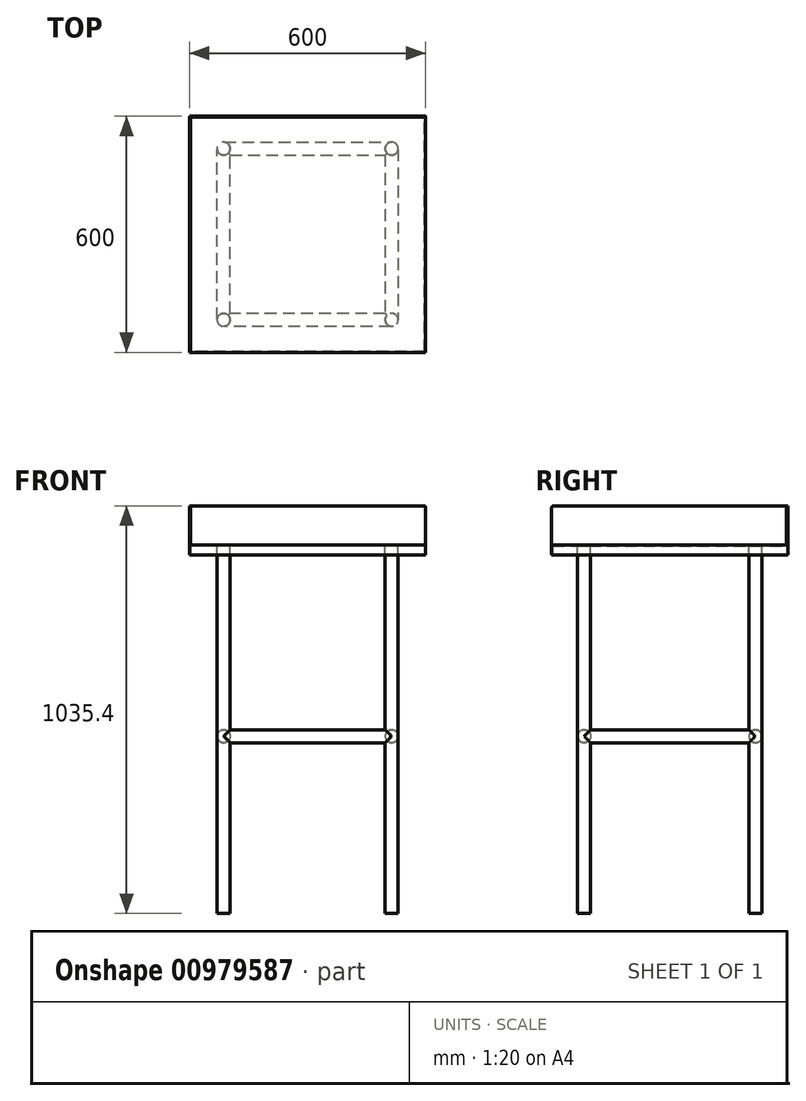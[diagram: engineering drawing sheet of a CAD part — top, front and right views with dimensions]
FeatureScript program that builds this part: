
annotation { "Feature Type Name" : "Feature", "Feature Type Description" : "" }
export const myFeature = defineFeature(function(context is Context, id is Id, definition is map)
    precondition{}
    {
        {
            var Q0;
            Q0=qCreatedBy(makeId("Top.planeOp"),FACE);
            var sketch = newSketch(context, id + "F0", { "sketchPlane" : qUnion([Q0])});
            skLineSegment(sketch, "E0.bottom", {"start": v(300, -300) * mm, "end": v(-300, -300) * mm});
            skLineSegment(sketch, "E0.top", {"start": v(300, 300) * mm, "end": v(-300, 300) * mm});
            skLineSegment(sketch, "E0.left", {"start": v(300, -300) * mm, "end": v(300, 300) * mm});
            skLineSegment(sketch, "E0.right", {"start": v(-300, -300) * mm, "end": v(-300, 300) * mm});
            skPoint(sketch, "E0.middle", {"position": v(0, 0) * mm});
            skSolve(sketch);
        }
        {
            var Q0;
            Q0 = qSketchRegion(id + "F0", true);
            extrude(context, id + "F1", {"entities" : qUnion([Q0]), "depth" : 25.4 * mm, "offsetDistance" : 25.4 * mm});
        }
        {
            var Q0;
            Q0=makeQuery(id+"F1.opExtrude","CAP_FACE",FACE,{"disambiguationData":[OSD([sQuery(id+"F0.wireOp",EDGE,"E0.bottom"),sQuery(id+"F0.wireOp",EDGE,"E0.top"),sQuery(id+"F0.wireOp",EDGE,"E0.left"),sQuery(id+"F0.wireOp",EDGE,"E0.right")])],"isStart":true});
            shell(context, id + "F2", {"entities" : qUnion([Q0]), "thickness" : 2.54 * mm});
        }
        {
            var Q0;
            Q0=makeQuery(id+"F1.opExtrude","CAP_FACE",FACE,{"disambiguationData":[OSD([sQuery(id+"F0.wireOp",EDGE,"E0.bottom"),sQuery(id+"F0.wireOp",EDGE,"E0.top"),sQuery(id+"F0.wireOp",EDGE,"E0.left"),sQuery(id+"F0.wireOp",EDGE,"E0.right")])],"isStart":true});
            var sketch = newSketch(context, id + "F3", { "sketchPlane" : qUnion([Q0])});
            skCircle(sketch, "E1", {"center": v(213.5, -217.5) * mm, "radius": 16.5 * mm});
            skCircle(sketch, "E2", {"center": v(-213.5, -217.5) * mm, "radius": 16.5 * mm});
            skCircle(sketch, "E3", {"center": v(213.5, 217.5) * mm, "radius": 16.5 * mm});
            skCircle(sketch, "E4", {"center": v(-213.5, 217.5) * mm, "radius": 16.5 * mm});
            skSolve(sketch);
        }
        {
            var Q0;
            Q0 = qSketchRegion(id + "F3", true);
            extrude(context, id + "F4", {"entities" : qUnion([Q0]), "operationType" : NewBodyOperationType.ADD, "depth" : 910 * mm, "offsetDistance" : 25.4 * mm, "hasSecondDirection" : true, "secondDirectionBound" : SecondDirectionBoundingType.UP_TO_NEXT, "secondDirectionOppositeDirection" : true, "secondDirectionDepth" : 25.4 * mm});
        }
        {
            var Q0;
            Q0=makeQuery(id+"F1.opExtrude","CAP_FACE",FACE,{"disambiguationData":[OSD([sQuery(id+"F0.wireOp",EDGE,"E0.bottom"),sQuery(id+"F0.wireOp",EDGE,"E0.top"),sQuery(id+"F0.wireOp",EDGE,"E0.left"),sQuery(id+"F0.wireOp",EDGE,"E0.right")])],"isStart":false});
            var sketch = newSketch(context, id + "F5", { "sketchPlane" : qUnion([Q0])});
            skLineSegment(sketch, "E5.bottom", {"start": v(-300, -300) * mm, "end": v(-297, -300) * mm});
            skLineSegment(sketch, "E5.top", {"start": v(-300, 300) * mm, "end": v(-297, 300) * mm});
            skLineSegment(sketch, "E5.left", {"start": v(-300, -300) * mm, "end": v(-300, 300) * mm});
            skLineSegment(sketch, "E5.right", {"start": v(-297, -300) * mm, "end": v(-297, 297) * mm});
            skLineSegment(sketch, "E6.bottom", {"start": v(-297, 300) * mm, "end": v(300, 300) * mm});
            skLineSegment(sketch, "E6.top", {"start": v(-297, 297) * mm, "end": v(300, 297) * mm});
            skLineSegment(sketch, "E6.right", {"start": v(300, 300) * mm, "end": v(300, 297) * mm});
            skSolve(sketch);
        }
        {
            var Q0;
            Q0 = qSketchRegion(id + "F5", true);
            extrude(context, id + "F6", {"entities" : qUnion([Q0]), "operationType" : NewBodyOperationType.ADD, "depth" : 100 * mm, "offsetDistance" : 25.4 * mm});
        }
        {
            var Q0;
            Q0=makeQuery(id+"F6.opExtrude","CAP_EDGE",EDGE,{"disambiguationData":[OSD([sQuery(id+"F5.wireOp",EDGE,"E6.right")])],"isStart":false});
            fillet(context, id + "F7", {"entities" : qUnion([Q0]), "radius" : 5.08 * mm, "tangentPropagation" : true, "allowEdgeOverflow" : false});
        }
        {
            var Q0;
            Q0=makeQuery(id+"F6.opExtrude","CAP_EDGE",EDGE,{"disambiguationData":[OSD([sQuery(id+"F5.wireOp",EDGE,"E5.bottom")])],"isStart":false});
            fillet(context, id + "F8", {"entities" : qUnion([Q0]), "radius" : 5.08 * mm, "tangentPropagation" : true, "allowEdgeOverflow" : false});
        }
        {
            var Q0;
            Q0=makeQuery(id+"F4.opExtrude","CAP_EDGE",EDGE,{"disambiguationData":[OSD([sQuery(id+"F3.wireOp",EDGE,"E2")])],"isStart":false});
            cPlane(context, id + "F9", {"entities" : qUnion([Q0]), "cplaneType" : CPlaneType.LINE_ANGLE, "offset" : 25.4 * mm, "angle" : 90 * degree, "width" : 152.4 * mm, "height" : 152.4 * mm});
        }
        {
            var Q0;
            Q0=qCreatedBy(id+"F9.planeOp",FACE);
            var sketch = newSketch(context, id + "F10", { "sketchPlane" : qUnion([Q0])});
            skCircle(sketch, "E7", {"center": v(213.49, -460) * mm, "radius": 16.5 * mm});
            skSolve(sketch);
        }
        {
            var Q0;
            Q0 = qSketchRegion(id + "F10", true);
            extrude(context, id + "F11", {"entities" : qUnion([Q0]), "operationType" : NewBodyOperationType.ADD, "oppositeDirection" : true, "depth" : 433.32 * mm, "offsetDistance" : 25.4 * mm});
        }
        {
            var Q0;
            Q0=makeQuery(id+"F4.opExtrude","CAP_EDGE",EDGE,{"disambiguationData":[OSD([sQuery(id+"F3.wireOp",EDGE,"E4")])],"isStart":false});
            cPlane(context, id + "F12", {"entities" : qUnion([Q0]), "cplaneType" : CPlaneType.LINE_ANGLE, "offset" : 25.4 * mm, "angle" : 0 * degree, "width" : 152.4 * mm, "height" : 152.4 * mm});
        }
        {
            var Q0;
            Q0=qCreatedBy(id+"F12.planeOp",FACE);
            var sketch = newSketch(context, id + "F13", { "sketchPlane" : qUnion([Q0])});
            skCircle(sketch, "E8", {"center": v(217.47, -460) * mm, "radius": 16.5 * mm});
            skSolve(sketch);
        }
        {
            var Q0;
            Q0 = qSketchRegion(id + "F13", true);
            extrude(context, id + "F14", {"entities" : qUnion([Q0]), "operationType" : NewBodyOperationType.ADD, "oppositeDirection" : true, "depth" : 424.43 * mm, "offsetDistance" : 25.4 * mm});
        }
        {
            var Q0;
            Q0=makeQuery(id+"F4.opExtrude","CAP_EDGE",EDGE,{"disambiguationData":[OSD([sQuery(id+"F3.wireOp",EDGE,"E3")])],"isStart":false});
            cPlane(context, id + "F15", {"entities" : qUnion([Q0]), "cplaneType" : CPlaneType.LINE_ANGLE, "offset" : 25.4 * mm, "angle" : 90 * degree, "width" : 152.4 * mm, "height" : 152.4 * mm});
        }
        {
            var Q0;
            Q0=qCreatedBy(id+"F15.planeOp",FACE);
            var sketch = newSketch(context, id + "F16", { "sketchPlane" : qUnion([Q0])});
            skCircle(sketch, "E9", {"center": v(-213.5, -460) * mm, "radius": 16.5 * mm});
            skSolve(sketch);
        }
        {
            var Q0;
            Q0 = qSketchRegion(id + "F16", true);
            extrude(context, id + "F17", {"entities" : qUnion([Q0]), "operationType" : NewBodyOperationType.ADD, "depth" : 433.07 * mm, "offsetDistance" : 25.4 * mm});
        }
        {
            var Q0;
            Q0=makeQuery(id+"F4.opExtrude","CAP_EDGE",EDGE,{"disambiguationData":[OSD([sQuery(id+"F3.wireOp",EDGE,"E1")])],"isStart":false});
            cPlane(context, id + "F18", {"entities" : qUnion([Q0]), "cplaneType" : CPlaneType.LINE_ANGLE, "offset" : 25.4 * mm, "angle" : 0 * degree, "width" : 152.4 * mm, "height" : 152.4 * mm});
        }
        {
            var Q0;
            Q0=qCreatedBy(id+"F18.planeOp",FACE);
            var sketch = newSketch(context, id + "F19", { "sketchPlane" : qUnion([Q0])});
            skCircle(sketch, "E10", {"center": v(-217.89, -460) * mm, "radius": 16.5 * mm});
            skSolve(sketch);
        }
        {
            var Q0;
            Q0 = qSketchRegion(id + "F19", true);
            extrude(context, id + "F20", {"entities" : qUnion([Q0]), "operationType" : NewBodyOperationType.ADD, "depth" : 425.2 * mm, "offsetDistance" : 25.4 * mm});
        }
    });
